# Revit family: Скамейка стальная «Мадрид» Арт 12168
name_source: partatom
category: Антураж
revit_build: Autodesk Revit 2018 (Build: 20180423_1000(x64)
units: mm (PartAtom-declared; Revit-internal decimal feet)

## family parameters
Всегда вертикально = Да
Источник визуального образа = Геометрия семейства
На основе рабочей плоскости = Нет
Общий = Нет
При загрузке вырезать с полостями = Нет
Точка расчета площади = Нет

## types (9) — shared parameters
URL = https://hobbyka.ru
Артикул товара = Арт. 12168
Высота = 860 мм
Группа модели = Скамейки
Изготовитель = ООО «Хоббика»
Изображение типоразмера = Скамейка стальная «Мадрид» Арт 12168.jpg
Материал изделия = Сталь, дерево, композитные материалы
Ширина = 600 мм

## per-type parameters (varying)
| type | Версия 0,6 м (кресло) | Версия 1,5 м | Версия 1,5 м композит | Версия 1,5 м нержавейка плюс сосна | Версия 1,8 м | Версия 1,8 м композит | Версия 2,0 м (3 опоры) | Версия 2,0 м (3 опоры) композит | Версия 3,0 м (3 опоры) | Длина | Описание | Средняя опора | Цвет лавки | Цвет опор |
| Версия 0,6 м (кресло) | Да | Нет | Нет | Нет | Нет | Нет | Нет | Нет | Нет | 600 мм | Скамейка стальная «Мадрид». Версия 0,6 м (кресло) | Нет | Дерево | Сталь |
| Версия 1,5 м | Нет | Да | Нет | Нет | Нет | Нет | Нет | Нет | Нет | 1500 мм | Скамейка стальная «Мадрид». Версия 1,5 м | Нет | Дерево | Сталь |
| Версия 1,5 м комопзит | Нет | Нет | Да | Нет | Нет | Нет | Нет | Нет | Нет | 1500 мм | Скамейка стальная «Мадрид». Версия 1,5 м. Материал лавки композит | Нет | Композит | Сталь |
| Версия 1,5 м нержавейка плюс сосна | Нет | Нет | Нет | Да | Нет | Нет | Нет | Нет | Нет | 1500 мм | Скамейка стальная «Мадрид». Версия 1,5 м. Материал опор нержавеющая стали, материал лавки сосна | Нет | Сосна | Нержавейка |
| Версия 1,8 м | Нет | Нет | Нет | Нет | Да | Нет | Нет | Нет | Нет | 1800 мм | Скамейка стальная «Мадрид». Версия 1,8 м | Нет | Дерево | Сталь |
| Версия 1,8 м композит | Нет | Нет | Нет | Нет | Нет | Да | Нет | Нет | Нет | 1800 мм | Скамейка стальная «Мадрид». Версия 1,8 м. Материал лавки композит | Нет | Композит | Сталь |
| Версия 2,0 м (3 опоры) | Нет | Нет | Нет | Нет | Нет | Нет | Да | Нет | Нет | 2000 мм | Скамейка стальная «Мадрид». Версия 2,0 м. На трех опорах | Да | Дерево | Сталь |
| Версия 2,0 м (3 опоры) композит | Нет | Нет | Нет | Нет | Нет | Нет | Нет | Да | Нет | 2000 мм | Скамейка стальная «Мадрид». Версия 2,0 м, Материал лавки композит, на трех опорах | Да | Композит | Сталь |
| Версия 3,0 м (3 опоры) | Нет | Нет | Нет | Нет | Нет | Нет | Нет | Нет | Да | 3000 мм | Скамейка стальная «Мадрид». Версия 3,0 м. На трех опорах | Да | Дерево | Сталь |
